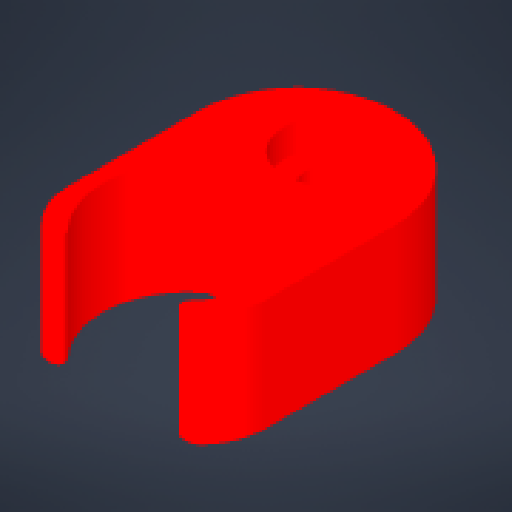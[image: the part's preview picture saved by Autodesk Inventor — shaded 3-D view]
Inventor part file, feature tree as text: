
AUTODESK INVENTOR PART (.ipt)
format: ipt  version: 2023.4 (Build 274418000, 418)  size: 245,248 bytes
history: native  units: mm
features: reference x6, other x4, sketch x2, extrude x2, plane x1, projected_geometry x1
ambient origin geometry x8: Origin, YZ Plane, XZ Plane, XY Plane, X Axis, Y Axis, Z Axis, Center Point
bodies: Solid1 (feature_tree)
feature tree (16):
  sketch  "Sketch1"  dims[d3=6.0mm d4=0.0mm d10=6.0mm]
  plane  "Work Plane1"
  extrude  "Extrusion1"  Depth=6.0mm
  extrude  "Extrusion2"  Depth=1.0mm
  reference  "Reference1"
  reference  "Reference2"
  reference  "Reference3"
  reference  "Reference4"
  reference  "Reference5"
  reference  "Reference6"
  sketch  "Sketch2"  dims[d11=2.0mm d12=0.0mm d18=1.0mm d20=3.0mm d21=6.0mm d22=10.0mm d24=0.5mm d25=0.0mm d26=0.0mm d27=0.0mm]
  projected_geometry  "Projected Loop1"
  parser-record x1  (decoder bookkeeping rows leaked as tree rows — omitted from the tree; the rows remain in map.json)
  other  "XYZ Stage V5.iam"
  other  "Z Stage Body V5:1"
  other  "DC Motor:1"
note: 1 file-system path scrubbed to <path> (originals preserved in map.json)
